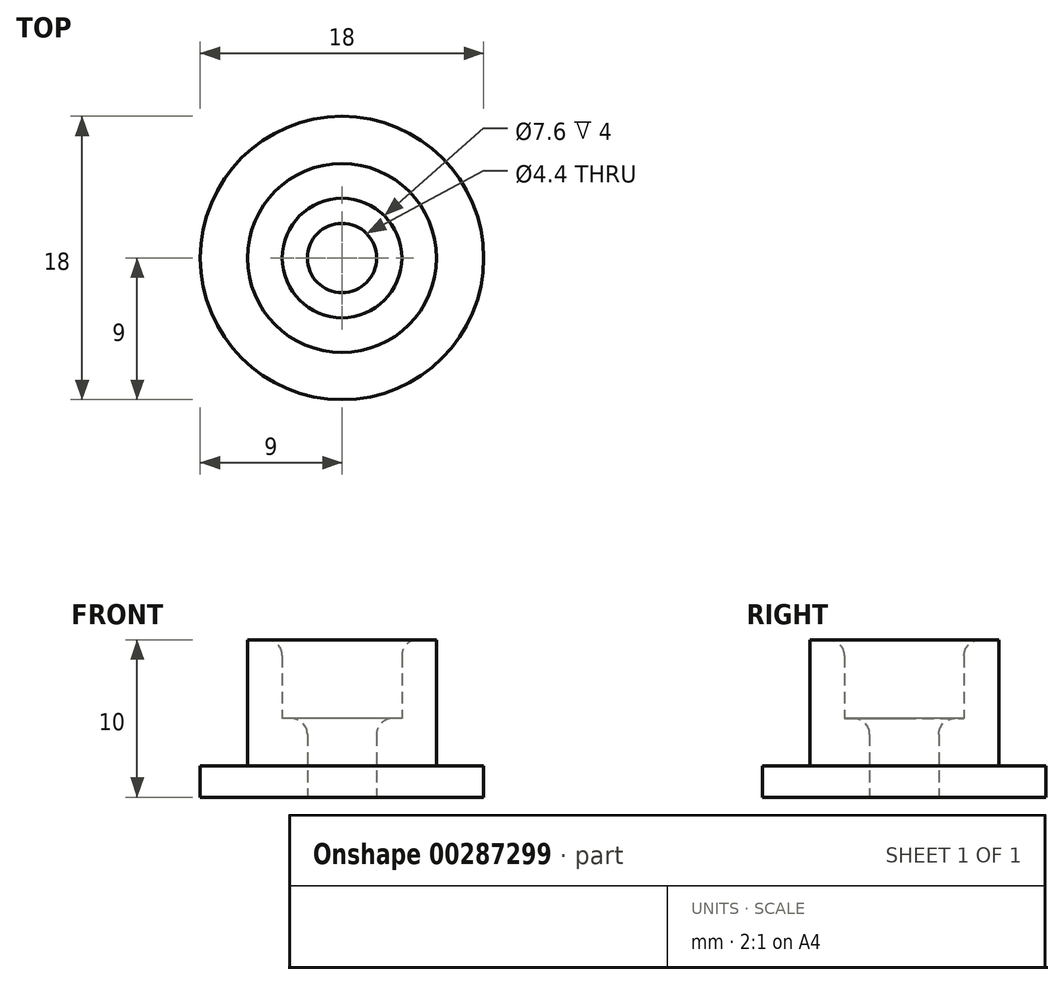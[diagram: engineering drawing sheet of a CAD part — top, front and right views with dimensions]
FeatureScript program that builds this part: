
annotation { "Feature Type Name" : "Feature", "Feature Type Description" : "" }
export const myFeature = defineFeature(function(context is Context, id is Id, definition is map)
    precondition{}
    {
        {
            var Q0;
            Q0=qCreatedBy(makeId("Top.planeOp"),FACE);
            var sketch = newSketch(context, id + "F0", { "sketchPlane" : qUnion([Q0])});
            skCircle(sketch, "E0", {"center": v(0, 0) * mm, "radius": 6 * mm});
            skCircle(sketch, "E1", {"center": v(0, 0) * mm, "radius": 9 * mm});
            skCircle(sketch, "E2", {"center": v(0, 0) * mm, "radius": 2.2 * mm});
            skCircle(sketch, "E3", {"center": v(0, 0) * mm, "radius": 3.8 * mm});
            skSolve(sketch);
        }
        {
            var Q0;
            Q0=qSketchRegion(id+"F0",true);
            extrude(context, id + "F1", {"entities" : qUnion([Q0]), "depth" : 2 * mm});
        }
        {
            var Q0;
            Q0=makeQuery(id+"F0.imprint","IMPRINT",FACE,{"disambiguationData":[TD([[makeQuery(id+"F0.imprint","IMPRINT",EDGE,{"derivedFrom":sQuery(id+"F0.wireOp",EDGE,"E0")}),1.0]])]});
            extrude(context, id + "F2", {"entities" : qUnion([Q0]), "operationType" : NewBodyOperationType.ADD, "depth" : 10 * mm});
        }
        {
            var Q0;
            Q0=makeQuery(id+"F0.imprint","IMPRINT",FACE,{"disambiguationData":[TD([[makeQuery(id+"F0.imprint","IMPRINT",EDGE,{"derivedFrom":sQuery(id+"F0.wireOp",EDGE,"E2")}),-1.0]])]});
            extrude(context, id + "F3", {"entities" : qUnion([Q0]), "operationType" : NewBodyOperationType.ADD, "depth" : 5 * mm});
        }
        {
            var Q0;
            Q0=makeQuery(id+"F2.opExtrude","CAP_EDGE",EDGE,{"disambiguationData":[OSD([sQuery(id+"F0.wireOp",EDGE,"E3")])],"isStart":false});
            fillet(context, id + "F4", {"entities" : qUnion([Q0]), "radius" : 1 * mm, "tangentPropagation" : true, "allowEdgeOverflow" : false});
        }
        {
            var Q0;
            Q0=makeQuery(id+"F3.opExtrude","CAP_EDGE",EDGE,{"disambiguationData":[OSD([sQuery(id+"F0.wireOp",EDGE,"E2")])],"isStart":false});
            fillet(context, id + "F5", {"entities" : qUnion([Q0]), "radius" : 1 * mm, "tangentPropagation" : true, "allowEdgeOverflow" : false});
        }
    });
